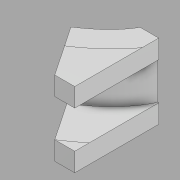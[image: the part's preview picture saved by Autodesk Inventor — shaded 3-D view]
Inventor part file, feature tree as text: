
AUTODESK INVENTOR PART (.ipt)
format: ipt  version: 2022.2 (Build 262287010, 287A)  size: 144,384 bytes
history: native  units: in
note: dims shown in document units (in); Inventor stores cm internally (conversion verified against a paired STEP export)
features: extrude x1, sketch x1, other x1
ambient origin geometry x8: Origin, YZ Plane, XZ Plane, XY Plane, X Axis, Y Axis, Z Axis, Center Point
bodies: Solid1 (feature_tree)
feature tree (3):
  extrude  "Extrusion1"  [1 undecoded]
  sketch  "Sketch1"  dims[d0=1.0in d1=0.0in]
  other  "Front (8)"
note: 1 required parameter value undecoded (feature->parameter linkage not recoverable at this tier; creation-order binding heuristic only, values carry confidence <= 0.55)
